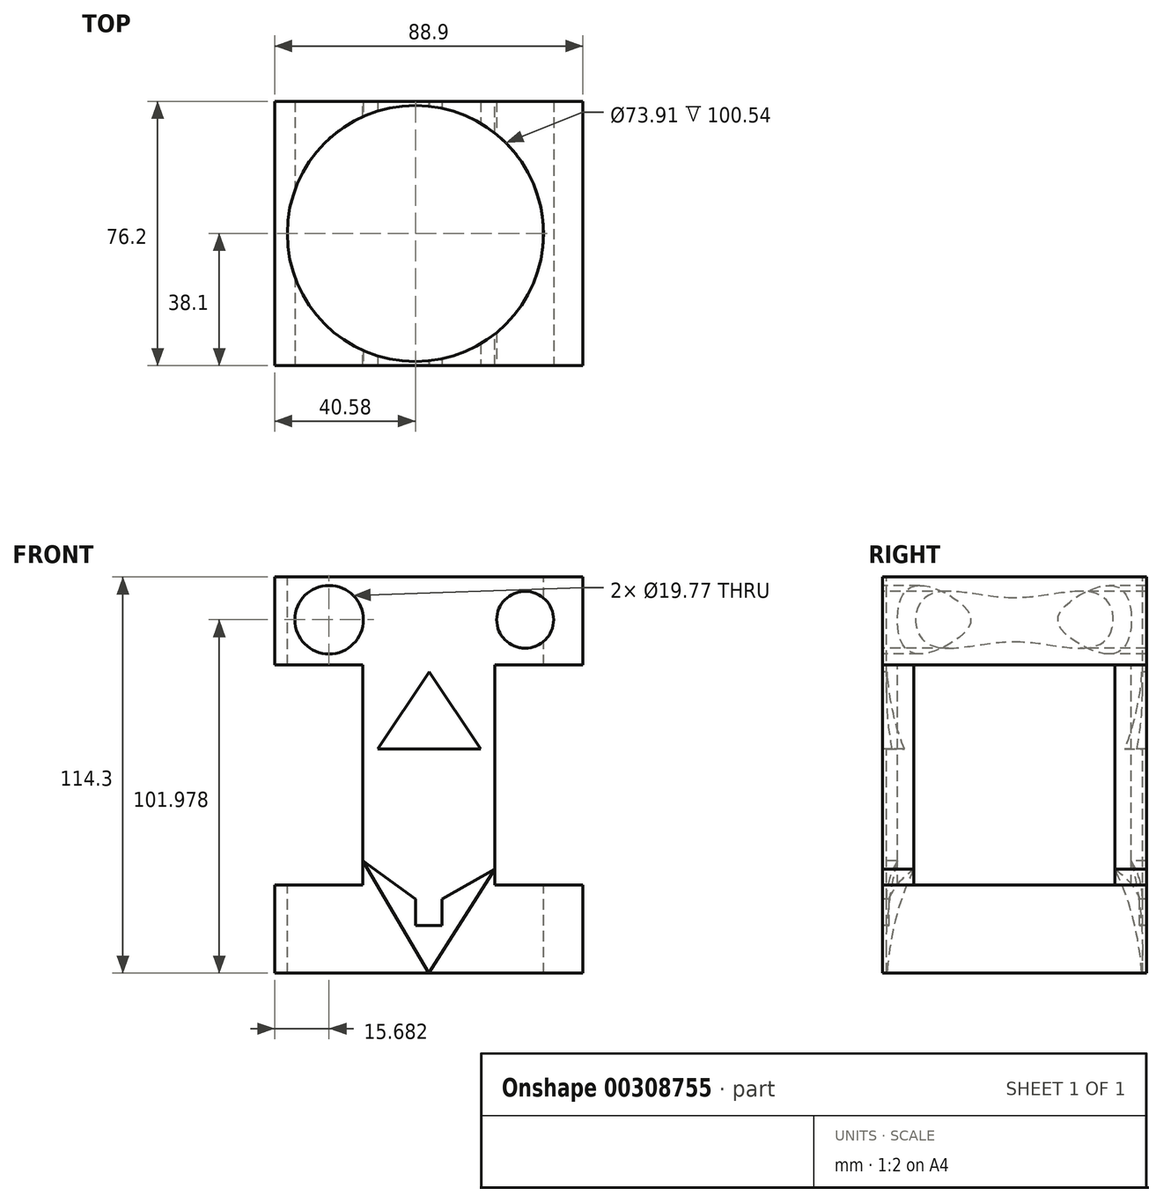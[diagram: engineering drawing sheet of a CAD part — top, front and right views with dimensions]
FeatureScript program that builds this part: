
annotation { "Feature Type Name" : "Feature", "Feature Type Description" : "" }
export const myFeature = defineFeature(function(context is Context, id is Id, definition is map)
    precondition{}
    {
        {
            var Q0;
            Q0=qCreatedBy(makeId("Front.planeOp"),FACE);
            var sketch = newSketch(context, id + "F0", { "sketchPlane" : qUnion([Q0])});
            skLineSegment(sketch, "E0", {"start": v(-40.58, -55.23) * mm, "end": v(48.32, -55.23) * mm});
            skLineSegment(sketch, "E1", {"start": v(48.32, -55.23) * mm, "end": v(48.32, -29.83) * mm});
            skLineSegment(sketch, "E2", {"start": v(48.32, -29.83) * mm, "end": v(22.92, -29.83) * mm});
            skLineSegment(sketch, "E3", {"start": v(22.92, -29.83) * mm, "end": v(22.92, 33.67) * mm});
            skLineSegment(sketch, "E4", {"start": v(22.92, 33.67) * mm, "end": v(48.32, 33.67) * mm});
            skLineSegment(sketch, "E5", {"start": v(48.32, 33.67) * mm, "end": v(48.32, 59.07) * mm});
            skLineSegment(sketch, "E6", {"start": v(48.32, 59.07) * mm, "end": v(-40.58, 59.07) * mm});
            skLineSegment(sketch, "E7", {"start": v(-40.58, 59.07) * mm, "end": v(-40.58, 33.67) * mm});
            skLineSegment(sketch, "E8", {"start": v(-40.58, 33.67) * mm, "end": v(-15.18, 33.67) * mm});
            skLineSegment(sketch, "E9", {"start": v(-15.18, 33.67) * mm, "end": v(-15.18, -29.83) * mm});
            skLineSegment(sketch, "E10", {"start": v(-15.18, -29.83) * mm, "end": v(-40.58, -29.83) * mm});
            skLineSegment(sketch, "E11", {"start": v(-40.58, -29.83) * mm, "end": v(-40.58, -55.23) * mm});
            skSolve(sketch);
        }
        {
            var Q0;
            Q0 = qSketchRegion(id + "F0", true);
            extrude(context, id + "F1", {"entities" : qUnion([Q0]), "depth" : 76.2 * mm});
        }
        {
            var Q0;
            Q0=makeQuery(id+"F1.opExtrude","SWEPT_FACE",FACE,{"disambiguationData":[OSD([sQuery(id+"F0.wireOp",EDGE,"E3")])]});
            var sketch = newSketch(context, id + "F2", { "sketchPlane" : qUnion([Q0])});
            skCircle(sketch, "E12", {"center": v(-38.1, 0) * mm, "radius": 23.9 * mm});
            skPoint(sketch, "E12.centerSnap0", {"position": v(-38.1, 33.67) * mm});
            skSolve(sketch);
        }
        {
            var Q0;
            Q0=makeQuery(id+"F2.imprint","IMPRINT",FACE,{"disambiguationData":[TD([[makeQuery(id+"F2.imprint","IMPRINT",EDGE,{"derivedFrom":sQuery(id+"F2.wireOp",EDGE,"E12")}),1.0]])]});
            extrude(context, id + "F3", {"entities" : qUnion([Q0]), "operationType" : NewBodyOperationType.REMOVE, "endBound" : BoundingType.THROUGH_ALL, "oppositeDirection" : true, "depth" : 25.4 * mm});
        }
        {
            var Q0;
            Q0=makeQuery(id+"F1.opExtrude","CAP_FACE",FACE,{"disambiguationData":[OSD([sQuery(id+"F0.wireOp",EDGE,"E0"),sQuery(id+"F0.wireOp",EDGE,"E1"),sQuery(id+"F0.wireOp",EDGE,"E2"),sQuery(id+"F0.wireOp",EDGE,"E3"),sQuery(id+"F0.wireOp",EDGE,"E4"),sQuery(id+"F0.wireOp",EDGE,"E5"),sQuery(id+"F0.wireOp",EDGE,"E6"),sQuery(id+"F0.wireOp",EDGE,"E7"),sQuery(id+"F0.wireOp",EDGE,"E8"),sQuery(id+"F0.wireOp",EDGE,"E9"),sQuery(id+"F0.wireOp",EDGE,"E10"),sQuery(id+"F0.wireOp",EDGE,"E11")])],"isStart":false});
            var sketch = newSketch(context, id + "F4", { "sketchPlane" : qUnion([Q0])});
            skLineSegment(sketch, "E13", {"start": v(-10.83, 9.44) * mm, "end": v(4.02, 31.73) * mm});
            skLineSegment(sketch, "E14", {"start": v(4.02, 31.73) * mm, "end": v(18.88, 9.44) * mm});
            skLineSegment(sketch, "E15", {"start": v(18.88, 9.44) * mm, "end": v(-10.83, 9.44) * mm});
            skSolve(sketch);
        }
        {
            var Q0;
            Q0=makeQuery(id+"F4.imprint","IMPRINT",FACE,{"disambiguationData":[TD([[makeQuery(id+"F4.imprint","IMPRINT",EDGE,{"derivedFrom":sQuery(id+"F4.wireOp",EDGE,"E13")}),-1.0]])]});
            extrude(context, id + "F5", {"entities" : qUnion([Q0]), "operationType" : NewBodyOperationType.REMOVE, "endBound" : BoundingType.THROUGH_ALL, "oppositeDirection" : true, "depth" : 25.4 * mm});
        }
        {
            var Q0;
            Q0=makeQuery(id+"F1.opExtrude","SWEPT_FACE",FACE,{"disambiguationData":[OSD([sQuery(id+"F0.wireOp",EDGE,"E6")])]});
            var sketch = newSketch(context, id + "F6", { "sketchPlane" : qUnion([Q0])});
            skCircle(sketch, "E16", {"center": v(0, -38.1) * mm, "radius": 36.95 * mm});
            skPoint(sketch, "E16.centerSnap0", {"position": v(-40.58, -38.1) * mm});
            skSolve(sketch);
        }
        {
            var Q0;
            Q0=makeQuery(id+"F6.imprint","IMPRINT",FACE,{"disambiguationData":[TD([[makeQuery(id+"F6.imprint","IMPRINT",EDGE,{"derivedFrom":sQuery(id+"F6.wireOp",EDGE,"E16")}),1.0]])]});
            extrude(context, id + "F7", {"entities" : qUnion([Q0]), "operationType" : NewBodyOperationType.REMOVE, "endBound" : BoundingType.THROUGH_ALL, "oppositeDirection" : true, "depth" : 25.4 * mm});
        }
        {
            var Q0;
            Q0=makeQuery(id+"F1.opExtrude","CAP_FACE",FACE,{"disambiguationData":[OSD([sQuery(id+"F0.wireOp",EDGE,"E0"),sQuery(id+"F0.wireOp",EDGE,"E1"),sQuery(id+"F0.wireOp",EDGE,"E2"),sQuery(id+"F0.wireOp",EDGE,"E3"),sQuery(id+"F0.wireOp",EDGE,"E4"),sQuery(id+"F0.wireOp",EDGE,"E5"),sQuery(id+"F0.wireOp",EDGE,"E6"),sQuery(id+"F0.wireOp",EDGE,"E7"),sQuery(id+"F0.wireOp",EDGE,"E8"),sQuery(id+"F0.wireOp",EDGE,"E9"),sQuery(id+"F0.wireOp",EDGE,"E10"),sQuery(id+"F0.wireOp",EDGE,"E11")])],"isStart":false});
            var sketch = newSketch(context, id + "F8", { "sketchPlane" : qUnion([Q0])});
            skCircle(sketch, "E17", {"center": v(-24.9, 46.75) * mm, "radius": 9.88 * mm});
            skCircle(sketch, "E18", {"center": v(31.68, 46.75) * mm, "radius": 8.2 * mm});
            skSolve(sketch);
        }
        {
            var Q0;
            Q0=makeQuery(id+"F8.imprint","IMPRINT",FACE,{"disambiguationData":[TD([[makeQuery(id+"F8.imprint","IMPRINT",EDGE,{"derivedFrom":sQuery(id+"F8.wireOp",EDGE,"E17")}),1.0]])]});
            var Q1;
            Q1=makeQuery(id+"F8.imprint","IMPRINT",FACE,{"disambiguationData":[TD([[makeQuery(id+"F8.imprint","IMPRINT",EDGE,{"derivedFrom":sQuery(id+"F8.wireOp",EDGE,"E18")}),1.0]])]});
            extrude(context, id + "F9", {"entities" : qUnion([Q0, Q1]), "operationType" : NewBodyOperationType.REMOVE, "endBound" : BoundingType.THROUGH_ALL, "oppositeDirection" : true, "depth" : 25.4 * mm});
        }
        {
            var Q0;
            Q0=makeQuery(id+"F1.opExtrude","CAP_FACE",FACE,{"disambiguationData":[OSD([sQuery(id+"F0.wireOp",EDGE,"E0"),sQuery(id+"F0.wireOp",EDGE,"E1"),sQuery(id+"F0.wireOp",EDGE,"E2"),sQuery(id+"F0.wireOp",EDGE,"E3"),sQuery(id+"F0.wireOp",EDGE,"E4"),sQuery(id+"F0.wireOp",EDGE,"E5"),sQuery(id+"F0.wireOp",EDGE,"E6"),sQuery(id+"F0.wireOp",EDGE,"E7"),sQuery(id+"F0.wireOp",EDGE,"E8"),sQuery(id+"F0.wireOp",EDGE,"E9"),sQuery(id+"F0.wireOp",EDGE,"E10"),sQuery(id+"F0.wireOp",EDGE,"E11")])],"isStart":false});
            var sketch = newSketch(context, id + "F10", { "sketchPlane" : qUnion([Q0])});
            skLineSegment(sketch, "E19", {"start": v(-15.18, -22.77) * mm, "end": v(3.87, -55.23) * mm});
            skLineSegment(sketch, "E20", {"start": v(3.87, -55.23) * mm, "end": v(22.92, -25.17) * mm});
            skLineSegment(sketch, "E21", {"start": v(22.92, -25.17) * mm, "end": v(7.7, -33.8) * mm});
            skLineSegment(sketch, "E22", {"start": v(7.7, -33.8) * mm, "end": v(7.7, -41.47) * mm});
            skLineSegment(sketch, "E23", {"start": v(7.7, -41.47) * mm, "end": v(0, -41.47) * mm});
            skLineSegment(sketch, "E24", {"start": v(0, -41.47) * mm, "end": v(0, -33.8) * mm});
            skLineSegment(sketch, "E25", {"start": v(0, -33.8) * mm, "end": v(-15.18, -22.77) * mm});
            skSolve(sketch);
        }
        {
            var Q0;
            Q0=makeQuery(id+"F10.imprint","IMPRINT",FACE,{"disambiguationData":[TD([[makeQuery(id+"F10.imprint","IMPRINT",EDGE,{"derivedFrom":sQuery(id+"F10.wireOp",EDGE,"E19")}),1.0]])]});
            extrude(context, id + "F11", {"entities" : qUnion([Q0]), "operationType" : NewBodyOperationType.REMOVE, "endBound" : BoundingType.THROUGH_ALL, "oppositeDirection" : true, "depth" : 25.4 * mm});
        }
    });
